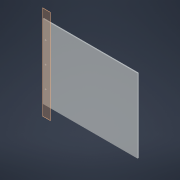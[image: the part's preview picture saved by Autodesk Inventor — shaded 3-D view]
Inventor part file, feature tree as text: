
AUTODESK INVENTOR PART (.ipt)
format: ipt  version: 2021 (Build 250183000, 183)  size: 103,424 bytes
history: native  units: mm
features: reference x4, other x3, extrude x2, sketch x2, plane x1
ambient origin geometry x8: Origin, YZ Plane, XZ Plane, XY Plane, X Axis, Y Axis, Z Axis, Center Point
bodies: Solid1 (feature_tree)
feature tree (12):
  plane  "Work Plane1"
  extrude  "Extrusion1"  Depth=3.0mm
  extrude  "Extrusion2"  Depth=3.0mm
  sketch  "Sketch1"  dims[d0=3.0mm d1=3.0mm]
  reference  "Reference1"
  sketch  "Sketch2"  dims[d2=250.0mm d3=20.0mm d4=3.0mm d5=0.0mm d6=0.0mm d7=0.0mm]
  reference  "Reference2"
  reference  "Reference3"
  reference  "Reference4"
  other  "<userpath>\green-house\green-house.iam"
  other  "green-house.iam"
  other  "frame:1"
